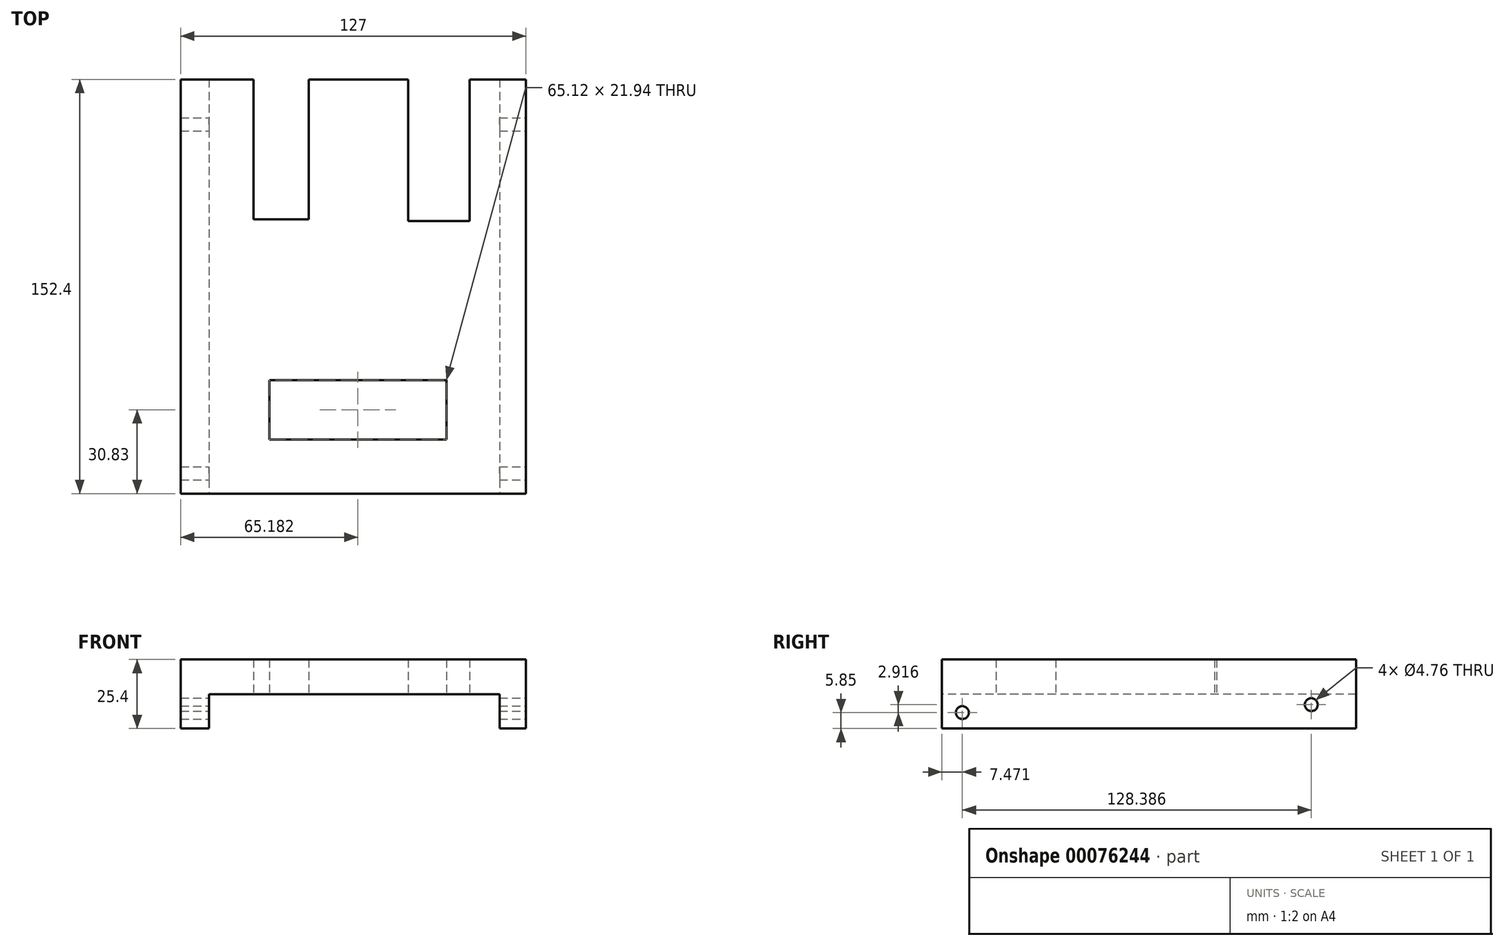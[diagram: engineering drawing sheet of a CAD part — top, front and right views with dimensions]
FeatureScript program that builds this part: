
annotation { "Feature Type Name" : "Feature", "Feature Type Description" : "" }
export const myFeature = defineFeature(function(context is Context, id is Id, definition is map)
    precondition{}
    {
        {
            var Q0;
            Q0=qCreatedBy(makeId("Front.planeOp"),FACE);
            var sketch = newSketch(context, id + "F0", { "sketchPlane" : qUnion([Q0])});
            skLineSegment(sketch, "E0.bottom", {"start": v(-68.54, 25.4) * mm, "end": v(58.46, 25.4) * mm});
            skLineSegment(sketch, "E0.top", {"start": v(-68.54, 0) * mm, "end": v(58.46, 0) * mm});
            skLineSegment(sketch, "E0.left", {"start": v(-68.54, 25.4) * mm, "end": v(-68.54, 0) * mm});
            skLineSegment(sketch, "E0.right", {"start": v(58.46, 25.4) * mm, "end": v(58.46, 0) * mm});
            skSolve(sketch);
        }
        {
            var Q0;
            Q0=makeQuery(id+"F0.imprint","IMPRINT",FACE,{"disambiguationData":[TD([[makeQuery(id+"F0.imprint","IMPRINT",EDGE,{"derivedFrom":sQuery(id+"F0.wireOp",EDGE,"E0.bottom")}),-1.0]])]});
            extrude(context, id + "F1", {"entities" : qUnion([Q0]), "depth" : 152.4 * mm});
        }
        {
            var Q0;
            Q0=makeQuery(id+"F1.opExtrude","CAP_FACE",FACE,{"disambiguationData":[OSD([sQuery(id+"F0.wireOp",EDGE,"E0.bottom"),sQuery(id+"F0.wireOp",EDGE,"E0.top"),sQuery(id+"F0.wireOp",EDGE,"E0.left"),sQuery(id+"F0.wireOp",EDGE,"E0.right")])],"isStart":false});
            var sketch = newSketch(context, id + "F2", { "sketchPlane" : qUnion([Q0])});
            skLineSegment(sketch, "E1.bottom", {"start": v(-58.07, 12.65) * mm, "end": v(48.77, 12.65) * mm});
            skLineSegment(sketch, "E1.top", {"start": v(-58.07, 0) * mm, "end": v(48.77, 0) * mm});
            skLineSegment(sketch, "E1.left", {"start": v(-58.07, 12.65) * mm, "end": v(-58.07, 0) * mm});
            skLineSegment(sketch, "E1.right", {"start": v(48.77, 12.65) * mm, "end": v(48.77, 0) * mm});
            skSolve(sketch);
        }
        {
            var Q0;
            Q0=makeQuery(id+"F2.imprint","IMPRINT",FACE,{"disambiguationData":[TD([[makeQuery(id+"F2.imprint","IMPRINT",EDGE,{"derivedFrom":sQuery(id+"F2.wireOp",EDGE,"E1.bottom")}),-1.0]])]});
            extrude(context, id + "F3", {"entities" : qUnion([Q0]), "operationType" : NewBodyOperationType.REMOVE, "endBound" : BoundingType.THROUGH_ALL, "oppositeDirection" : true, "depth" : 25.4 * mm});
        }
        {
            var Q0;
            Q0=makeQuery(id+"F1.opExtrude","SWEPT_FACE",FACE,{"disambiguationData":[OSD([sQuery(id+"F0.wireOp",EDGE,"E0.right")])]});
            var sketch = newSketch(context, id + "F4", { "sketchPlane" : qUnion([Q0])});
            skCircle(sketch, "E2", {"center": v(-16.54, 8.77) * mm, "radius": 2.38 * mm});
            skSolve(sketch);
        }
        {
            var Q0;
            Q0=makeQuery(id+"F4.imprint","IMPRINT",FACE,{"disambiguationData":[TD([[makeQuery(id+"F4.imprint","IMPRINT",EDGE,{"derivedFrom":sQuery(id+"F4.wireOp",EDGE,"E2")}),1.0]])]});
            extrude(context, id + "F5", {"entities" : qUnion([Q0]), "operationType" : NewBodyOperationType.REMOVE, "endBound" : BoundingType.THROUGH_ALL, "oppositeDirection" : true, "depth" : 25.4 * mm});
        }
        {
            var Q0;
            Q0=makeQuery(id+"F4.imprint","IMPRINT",FACE,{"disambiguationData":[TD([[makeQuery(id+"F4.imprint","IMPRINT",EDGE,{"derivedFrom":sQuery(id+"F4.wireOp",EDGE,"E2")}),-1.0]])]});
            var sketch = newSketch(context, id + "F6", { "sketchPlane" : qUnion([Q0])});
            skCircle(sketch, "E3", {"center": v(-144.93, 5.85) * mm, "radius": 2.38 * mm});
            skSolve(sketch);
        }
        {
            var Q0;
            Q0=makeQuery(id+"F6.imprint","IMPRINT",FACE,{"disambiguationData":[TD([[makeQuery(id+"F6.imprint","IMPRINT",EDGE,{"derivedFrom":sQuery(id+"F6.wireOp",EDGE,"E3")}),1.0]])]});
            extrude(context, id + "F7", {"entities" : qUnion([Q0]), "operationType" : NewBodyOperationType.REMOVE, "endBound" : BoundingType.THROUGH_ALL, "oppositeDirection" : true, "depth" : 25.4 * mm});
        }
        {
            var Q0;
            Q0=makeQuery(id+"F3.boolean.opBoolean","COPY",FACE,{"derivedFrom":makeQuery(id+"F3.opExtrude","SWEPT_FACE",FACE,{"disambiguationData":[OSD([sQuery(id+"F2.wireOp",EDGE,"E1.bottom")])]})});
            var sketch = newSketch(context, id + "F8", { "sketchPlane" : qUnion([Q0])});
            skLineSegment(sketch, "E4.bottom", {"start": v(15.2, 0) * mm, "end": v(37.75, 0) * mm});
            skLineSegment(sketch, "E4.top", {"start": v(15.2, 52.11) * mm, "end": v(37.75, 52.11) * mm});
            skLineSegment(sketch, "E4.left", {"start": v(15.2, 0) * mm, "end": v(15.2, 52.11) * mm});
            skLineSegment(sketch, "E4.right", {"start": v(37.75, 0) * mm, "end": v(37.75, 52.11) * mm});
            skSolve(sketch);
        }
        {
            var Q0;
            Q0=makeQuery(id+"F8.imprint","IMPRINT",FACE,{"disambiguationData":[TD([[makeQuery(id+"F8.imprint","IMPRINT",EDGE,{"derivedFrom":sQuery(id+"F8.wireOp",EDGE,"E4.bottom")}),1.0]])]});
            extrude(context, id + "F9", {"entities" : qUnion([Q0]), "operationType" : NewBodyOperationType.REMOVE, "endBound" : BoundingType.THROUGH_ALL, "oppositeDirection" : true, "depth" : 25.4 * mm});
        }
        {
            var Q0;
            Q0=makeQuery(id+"F3.boolean.opBoolean","COPY",FACE,{"derivedFrom":makeQuery(id+"F3.opExtrude","SWEPT_FACE",FACE,{"disambiguationData":[OSD([sQuery(id+"F2.wireOp",EDGE,"E1.bottom")])]})});
            var sketch = newSketch(context, id + "F10", { "sketchPlane" : qUnion([Q0])});
            skLineSegment(sketch, "E5.bottom", {"start": v(-21.43, 0) * mm, "end": v(-41.72, 0) * mm});
            skLineSegment(sketch, "E5.top", {"start": v(-21.43, 51.4) * mm, "end": v(-41.72, 51.4) * mm});
            skLineSegment(sketch, "E5.left", {"start": v(-21.43, 0) * mm, "end": v(-21.43, 51.4) * mm});
            skLineSegment(sketch, "E5.right", {"start": v(-41.72, 0) * mm, "end": v(-41.72, 51.4) * mm});
            skSolve(sketch);
        }
        {
            var Q0;
            Q0=makeQuery(id+"F10.imprint","IMPRINT",FACE,{"disambiguationData":[TD([[makeQuery(id+"F10.imprint","IMPRINT",EDGE,{"derivedFrom":sQuery(id+"F10.wireOp",EDGE,"E5.bottom")}),1.0]])]});
            extrude(context, id + "F11", {"entities" : qUnion([Q0]), "operationType" : NewBodyOperationType.REMOVE, "endBound" : BoundingType.THROUGH_ALL, "oppositeDirection" : true, "depth" : 25.4 * mm});
        }
        {
            var Q0;
            Q0=makeQuery(id+"F3.boolean.opBoolean","COPY",FACE,{"derivedFrom":makeQuery(id+"F3.opExtrude","SWEPT_FACE",FACE,{"disambiguationData":[OSD([sQuery(id+"F2.wireOp",EDGE,"E1.bottom")])]})});
            var sketch = newSketch(context, id + "F12", { "sketchPlane" : qUnion([Q0])});
            skLineSegment(sketch, "E6.bottom", {"start": v(29.2, 110.6) * mm, "end": v(-35.92, 110.6) * mm});
            skLineSegment(sketch, "E6.top", {"start": v(29.2, 132.54) * mm, "end": v(-35.92, 132.54) * mm});
            skLineSegment(sketch, "E6.left", {"start": v(29.2, 110.6) * mm, "end": v(29.2, 132.54) * mm});
            skLineSegment(sketch, "E6.right", {"start": v(-35.92, 110.6) * mm, "end": v(-35.92, 132.54) * mm});
            skSolve(sketch);
        }
        {
            var Q0;
            Q0=makeQuery(id+"F12.imprint","IMPRINT",FACE,{"disambiguationData":[TD([[makeQuery(id+"F12.imprint","IMPRINT",EDGE,{"derivedFrom":sQuery(id+"F12.wireOp",EDGE,"E6.bottom")}),-1.0]])]});
            extrude(context, id + "F13", {"entities" : qUnion([Q0]), "operationType" : NewBodyOperationType.REMOVE, "endBound" : BoundingType.THROUGH_ALL, "oppositeDirection" : true, "depth" : 25.4 * mm});
        }
    });
